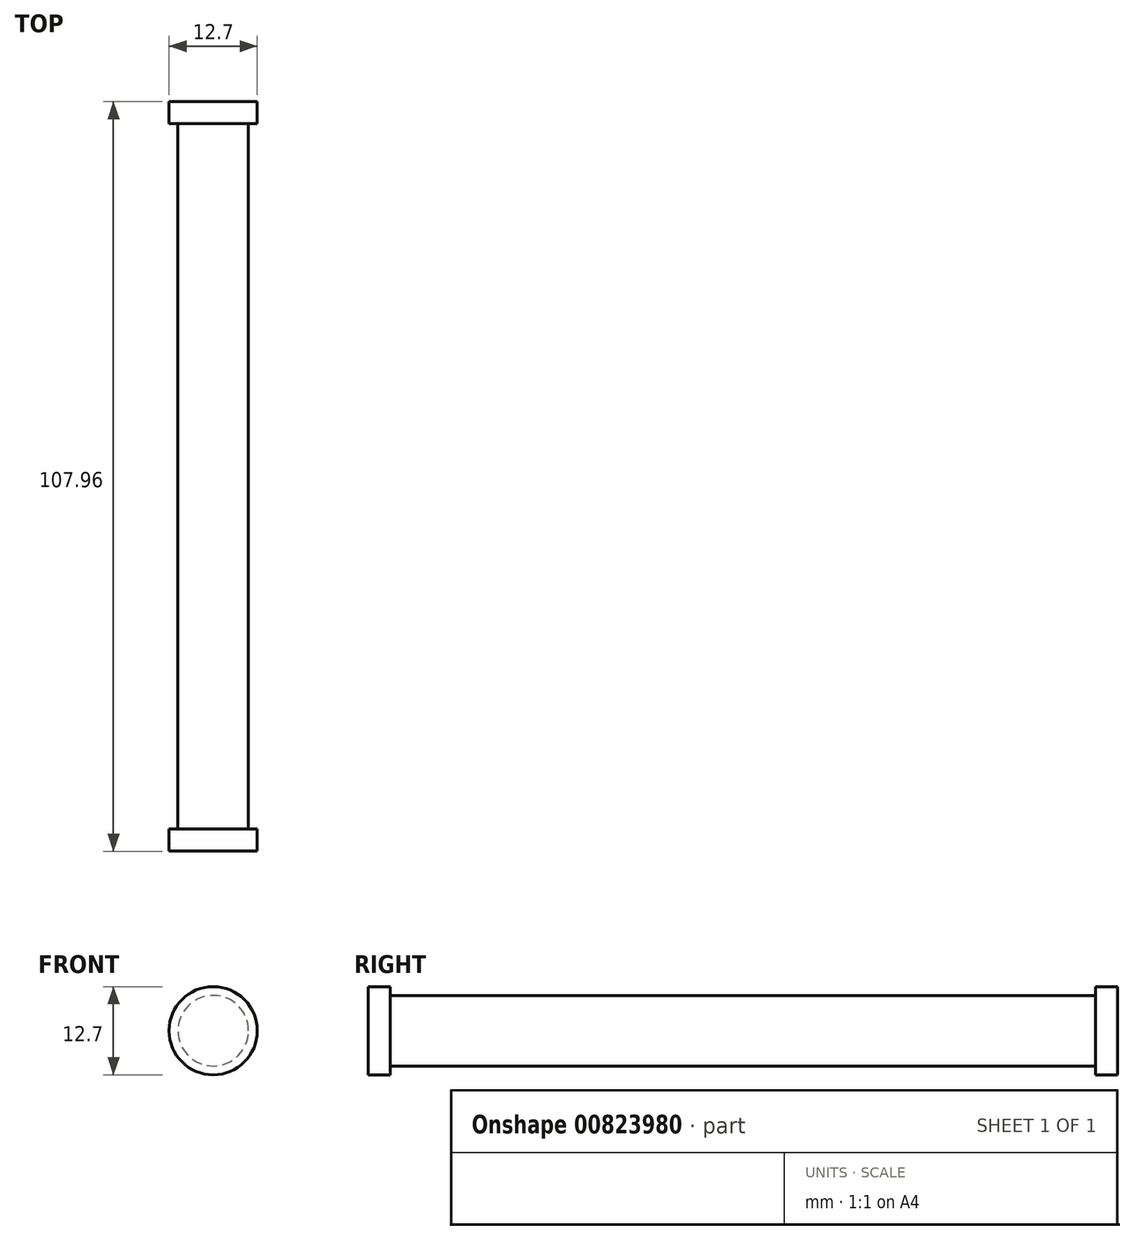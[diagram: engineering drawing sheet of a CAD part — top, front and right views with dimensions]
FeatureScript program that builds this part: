
annotation { "Feature Type Name" : "Feature", "Feature Type Description" : "" }
export const myFeature = defineFeature(function(context is Context, id is Id, definition is map)
    precondition{}
    {
        {
            var Q0;
            Q0=qCreatedBy(makeId("Front.planeOp"),FACE);
            var sketch = newSketch(context, id + "F0", { "sketchPlane" : qUnion([Q0])});
            skCircle(sketch, "E0", {"center": v(0, 0) * mm, "radius": 5.08 * mm});
            skSolve(sketch);
        }
        {
            var Q0;
            Q0=makeQuery(id+"F0.imprint","IMPRINT",FACE,{"disambiguationData":[TD([[makeQuery(id+"F0.imprint","IMPRINT",EDGE,{"derivedFrom":sQuery(id+"F0.wireOp",EDGE,"E0")}),1.0]])]});
            extrude(context, id + "F1", {"entities" : qUnion([Q0]), "endBound" : BoundingType.SYMMETRIC, "depth" : 101.6 * mm, "offsetDistance" : 25.4 * mm});
        }
        {
            var Q0;
            Q0=makeQuery(id+"F1.opExtrude","CAP_FACE",FACE,{"disambiguationData":[OSD([sQuery(id+"F0.wireOp",EDGE,"E0")])],"isStart":false});
            var sketch = newSketch(context, id + "F2", { "sketchPlane" : qUnion([Q0])});
            skCircle(sketch, "E1", {"center": v(0, 0) * mm, "radius": 6.35 * mm});
            skSolve(sketch);
        }
        {
            var Q0;
            Q0 = qSketchRegion(id + "F2", true);
            extrude(context, id + "F3", {"entities" : qUnion([Q0]), "operationType" : NewBodyOperationType.ADD, "depth" : 3.17 * mm, "offsetDistance" : 25.4 * mm});
        }
        {
            var Q0;
            Q0=makeQuery(id+"F1.opExtrude","CAP_FACE",FACE,{"disambiguationData":[OSD([sQuery(id+"F0.wireOp",EDGE,"E0")])],"isStart":true});
            var sketch = newSketch(context, id + "F4", { "sketchPlane" : qUnion([Q0])});
            skCircle(sketch, "E2", {"center": v(0, 0) * mm, "radius": 6.35 * mm});
            skSolve(sketch);
        }
        {
            var Q0;
            Q0 = qSketchRegion(id + "F4", true);
            extrude(context, id + "F5", {"entities" : qUnion([Q0]), "operationType" : NewBodyOperationType.ADD, "depth" : 3.17 * mm, "offsetDistance" : 25.4 * mm});
        }
    });
